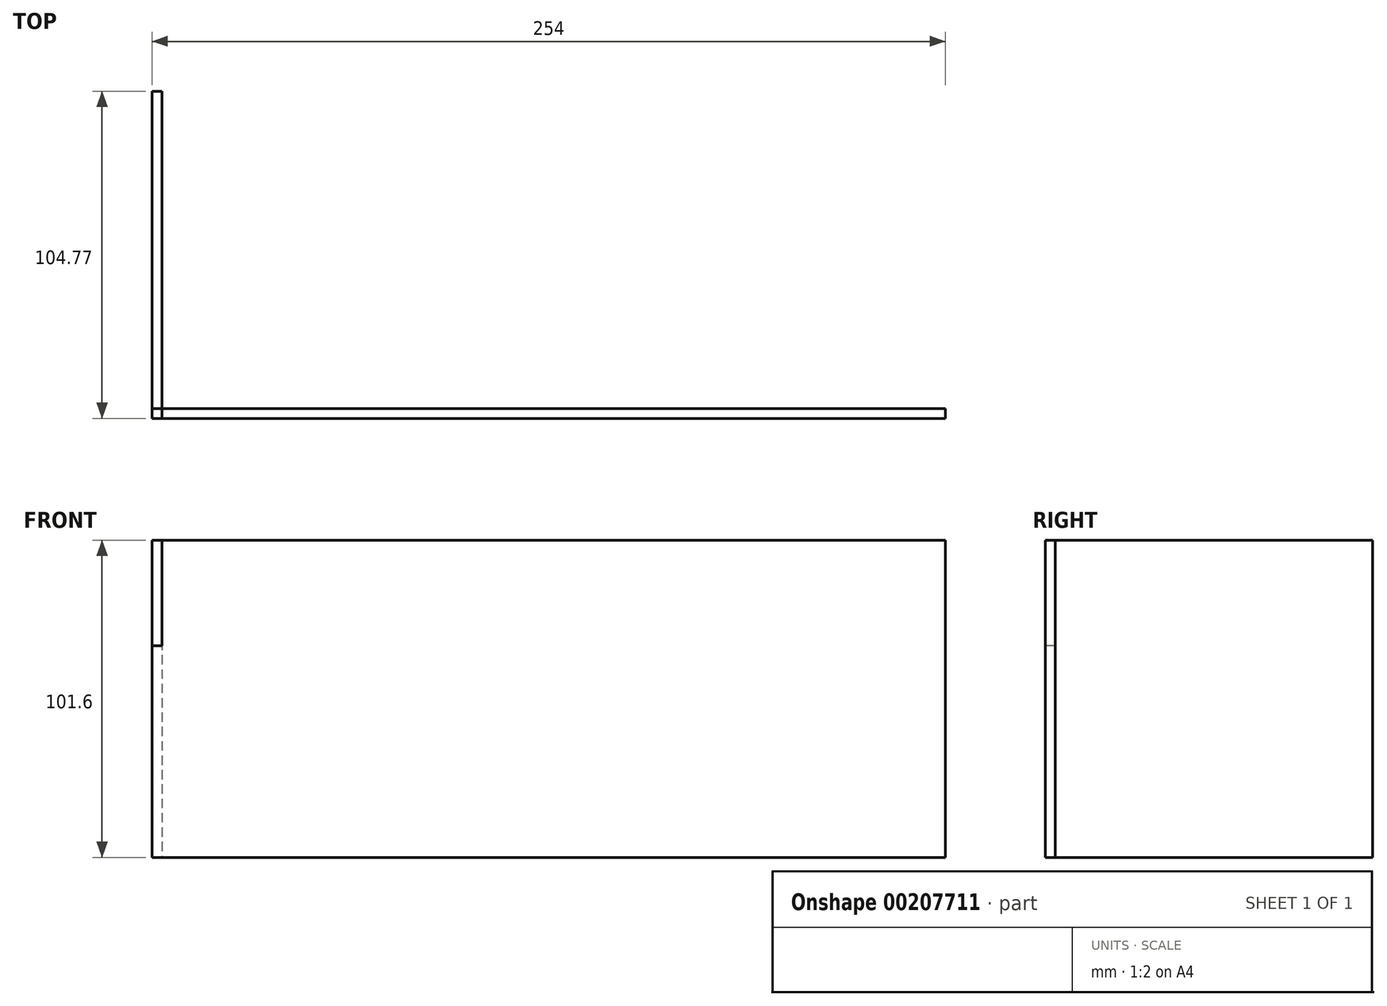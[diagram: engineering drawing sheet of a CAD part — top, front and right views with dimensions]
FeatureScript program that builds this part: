
annotation { "Feature Type Name" : "Feature", "Feature Type Description" : "" }
export const myFeature = defineFeature(function(context is Context, id is Id, definition is map)
    precondition{}
    {
        {
            var Q0;
            Q0=qCreatedBy(makeId("Front.planeOp"),FACE);
            var sketch = newSketch(context, id + "F0", { "sketchPlane" : qUnion([Q0])});
            skLineSegment(sketch, "E0.bottom", {"start": v(0, 50.8) * mm, "end": v(254, 50.8) * mm});
            skLineSegment(sketch, "E0.top", {"start": v(0, -50.8) * mm, "end": v(254, -50.8) * mm});
            skLineSegment(sketch, "E0.left", {"start": v(0, 50.8) * mm, "end": v(0, -50.8) * mm});
            skLineSegment(sketch, "E0.right", {"start": v(254, 50.8) * mm, "end": v(254, -50.8) * mm});
            skSolve(sketch);
        }
        {
            var Q0;
            Q0 = qSketchRegion(id + "F0", true);
            extrude(context, id + "F1", {"entities" : qUnion([Q0]), "depth" : 3.17 * mm});
        }
        {
            var Q0;
            Q0=qCreatedBy(makeId("Right.planeOp"),FACE);
            var sketch = newSketch(context, id + "F2", { "sketchPlane" : qUnion([Q0])});
            skLineSegment(sketch, "E1.bottom", {"start": v(0, 50.8) * mm, "end": v(101.6, 50.8) * mm});
            skLineSegment(sketch, "E1.top", {"start": v(0, -50.8) * mm, "end": v(101.6, -50.8) * mm});
            skLineSegment(sketch, "E1.left", {"start": v(0, 50.8) * mm, "end": v(0, -50.8) * mm});
            skLineSegment(sketch, "E1.right", {"start": v(101.6, 50.8) * mm, "end": v(101.6, -50.8) * mm});
            skSolve(sketch);
        }
        {
            var Q0;
            Q0 = qSketchRegion(id + "F2", true);
            extrude(context, id + "F3", {"entities" : qUnion([Q0]), "depth" : 3.17 * mm});
        }
        {
            var Q0;
            Q0=makeQuery(id+"F1.opExtrude","SWEPT_FACE",FACE,{"disambiguationData":[OSD([sQuery(id+"F0.wireOp",EDGE,"E0.left")])]});
            var sketch = newSketch(context, id + "F4", { "sketchPlane" : qUnion([Q0])});
            skLineSegment(sketch, "E2.bottom", {"start": v(0, 50.8) * mm, "end": v(3.18, 50.8) * mm});
            skLineSegment(sketch, "E2.top", {"start": v(0, 16.93) * mm, "end": v(3.17, 16.93) * mm});
            skLineSegment(sketch, "E2.left", {"start": v(0, 50.8) * mm, "end": v(0, 16.93) * mm});
            skLineSegment(sketch, "E2.right", {"start": v(3.18, 50.8) * mm, "end": v(3.18, 16.93) * mm});
            skLineSegment(sketch, "E3.bottom", {"start": v(3.17, 16.93) * mm, "end": v(0, 16.93) * mm});
            skLineSegment(sketch, "E3.top", {"start": v(3.17, -16.93) * mm, "end": v(0, -16.93) * mm});
            skLineSegment(sketch, "E3.left", {"start": v(3.18, 16.93) * mm, "end": v(3.18, -16.93) * mm});
            skLineSegment(sketch, "E3.right", {"start": v(0, 16.93) * mm, "end": v(0, -16.93) * mm});
            skLineSegment(sketch, "E4.bottom", {"start": v(0, -16.93) * mm, "end": v(3.17, -16.93) * mm});
            skLineSegment(sketch, "E4.top", {"start": v(0, -50.8) * mm, "end": v(3.18, -50.8) * mm});
            skLineSegment(sketch, "E4.left", {"start": v(0, -16.93) * mm, "end": v(0, -50.8) * mm});
            skLineSegment(sketch, "E4.right", {"start": v(3.18, -16.93) * mm, "end": v(3.18, -50.8) * mm});
            skSolve(sketch);
        }
        {
            var Q0;
            Q0=makeQuery(id+"F4.imprint","IMPRINT",FACE,{"disambiguationData":[TD([[makeQuery(id+"F4.imprint","IMPRINT",EDGE,{"derivedFrom":sQuery(id+"F4.wireOp",EDGE,"E2.bottom")}),1.0]])]});
            var Q1;
            Q1=makeQuery(id+"F4.imprint","IMPRINT",FACE,{"disambiguationData":[TD([[makeQuery(id+"F4.imprint","IMPRINT",EDGE,{"derivedFrom":sQuery(id+"F4.wireOp",EDGE,"E4.bottom")}),-1.0]])]});
            extrude(context, id + "F5", {"entities" : qUnion([Q0, Q1]), "oppositeDirection" : true, "depth" : 3.17 * mm});
        }
        {
            var Q0;
            Q0=makeQuery(id+"F5.opExtrude","SWEPT_BODY",BODY,{"disambiguationData":[OSD([sQuery(id+"F4.wireOp",EDGE,"E4.bottom"),sQuery(id+"F4.wireOp",EDGE,"E4.top"),sQuery(id+"F4.wireOp",EDGE,"E4.left"),sQuery(id+"F4.wireOp",EDGE,"E4.right")])]});
            var Q1;
            Q1=makeQuery(id+"F5.opExtrude","SWEPT_BODY",BODY,{"disambiguationData":[OSD([sQuery(id+"F4.wireOp",EDGE,"E2.bottom"),sQuery(id+"F4.wireOp",EDGE,"E2.left"),sQuery(id+"F4.wireOp",EDGE,"E2.right"),sQuery(id+"F4.wireOp",EDGE,"E3.bottom")])]});
            var Q2;
            Q2=makeQuery(id+"F1.opExtrude","SWEPT_BODY",BODY,{"disambiguationData":[OSD([sQuery(id+"F0.wireOp",EDGE,"E0.bottom"),sQuery(id+"F0.wireOp",EDGE,"E0.top"),sQuery(id+"F0.wireOp",EDGE,"E0.left"),sQuery(id+"F0.wireOp",EDGE,"E0.right")])]});
            booleanBodies(context, id + "F6", {"operationType" : BooleanOperationType.SUBTRACTION, "tools" : qUnion([Q0, Q1]), "targets" : qUnion([Q2]), "keepTools" : true});
        }
    });
